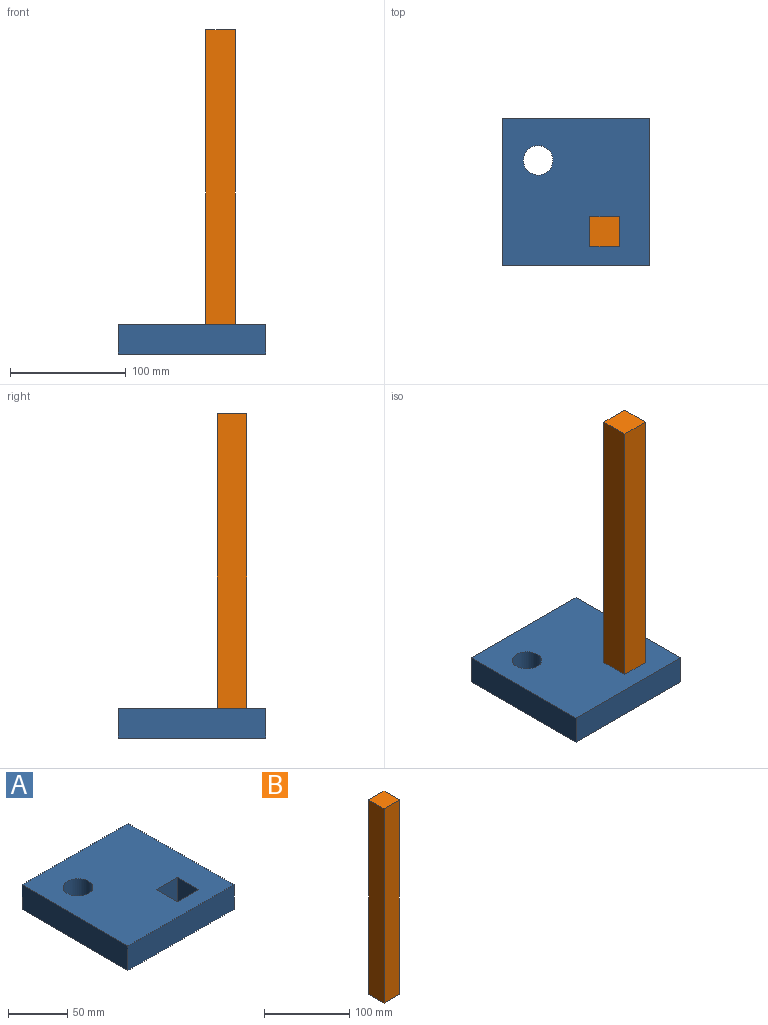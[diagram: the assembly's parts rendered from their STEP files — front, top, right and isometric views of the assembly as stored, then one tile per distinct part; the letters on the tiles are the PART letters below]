
ASSEMBLY  parts=2 mates=1
PART A: 11 faces, bbox 127x127x25.4 mm
  f0: plane 127x25.4mm, normal (0,-1,0), area 3225.8mm2, adj f1,f8,f9,f10
  f1: plane 127x25.4mm, normal (1,0,0), area 3225.8mm2, adj f0,f2,f9,f10
  f2: plane 127x25.4mm, normal (0,1,0), area 3225.8mm2, adj f1,f8,f9,f10
  f3: plane 25.4x25.4mm, normal (0,1,0), area 645.2mm2, adj f4,f6,f9,f10
  f4: plane 25.4x25.4mm, normal (1,0,0), area 645.2mm2, adj f3,f5,f9,f10
  f5: plane 25.4x25.4mm, normal (0,-1,0), area 645.2mm2, adj f4,f6,f9,f10
  f6: plane 25.4x25.4mm, normal (-1,0,0), area 645.2mm2, adj f3,f5,f9,f10
  f7: cylinder r=12.7mm len=25.4mm, axis (0,0,-1), area 2026.8mm2, adj f9,f10
  f8: plane 127x25.4mm, normal (-1,0,0), area 3225.8mm2, adj f0,f2,f9,f10
  f9: plane 127x127mm, normal (0,0,1), area 14977.1mm2, adj f0,f1,f2,f3,f4,f5,f6,f7
  f10: plane 127x127mm, normal (0,0,-1), area 14977.1mm2, adj f0,f1,f2,f3,f4,f5,f6,f7
PART B: 6 faces, bbox 25.4x25.4x279.4 mm
  f0: plane 279.4x25.4mm, normal (-1,0,0), area 7096.8mm2, adj f1,f3,f4,f5
  f1: plane 279.4x25.4mm, normal (0,-1,0), area 7096.8mm2, adj f0,f2,f4,f5
  f2: plane 279.4x25.4mm, normal (1,0,0), area 7096.8mm2, adj f1,f3,f4,f5
  f3: plane 279.4x25.4mm, normal (0,1,0), area 7096.8mm2, adj f0,f2,f4,f5
  f4: plane 25.4x25.4mm, normal (0,0,-1), area 645.2mm2, adj f0,f1,f2,f3
  f5: plane 25.4x25.4mm, normal (0,0,1), area 645.2mm2, adj f0,f1,f2,f3
PLACE A at identity fixed
PLACE B rot(axis=(0,0,-1),90deg) t=(-23.76,88.69,0)mm
MATE slider A.f10 <-> B.f5  axis (0,0,-1) through (11.94,-34.66,0)mm
